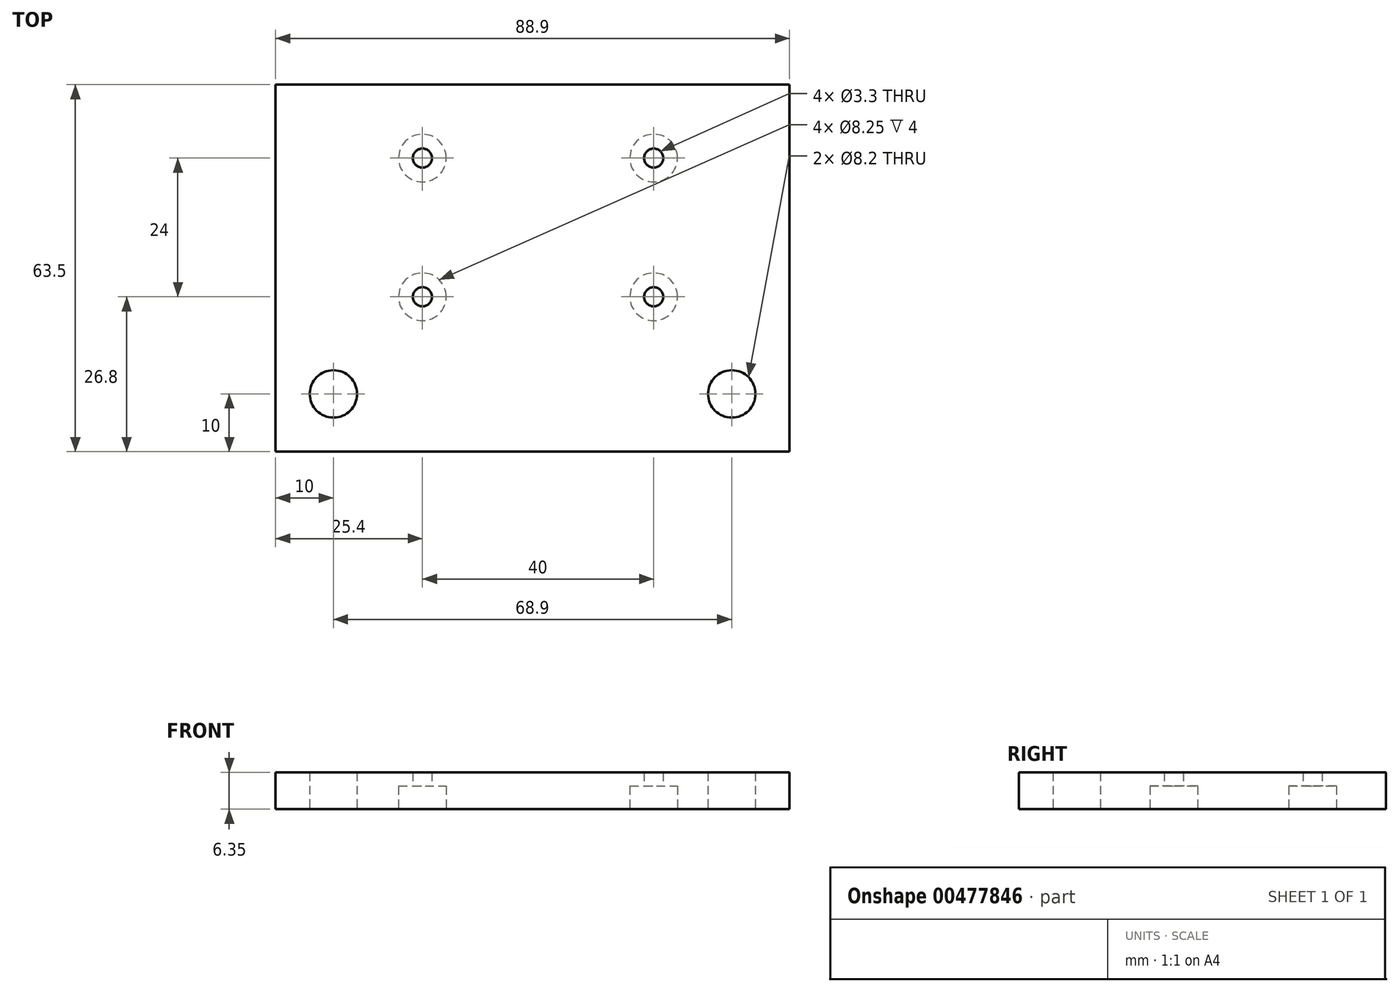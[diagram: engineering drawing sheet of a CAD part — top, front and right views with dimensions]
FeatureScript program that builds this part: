
annotation { "Feature Type Name" : "Feature", "Feature Type Description" : "" }
export const myFeature = defineFeature(function(context is Context, id is Id, definition is map)
    precondition{}
    {
        {
            var Q0;
            Q0=qCreatedBy(makeId("Top.planeOp"),FACE);
            var sketch = newSketch(context, id + "F0", { "sketchPlane" : qUnion([Q0])});
            skLineSegment(sketch, "E0.bottom", {"start": v(44.45, -31.75) * mm, "end": v(-44.45, -31.75) * mm});
            skLineSegment(sketch, "E0.top", {"start": v(44.45, 31.75) * mm, "end": v(-44.45, 31.75) * mm});
            skLineSegment(sketch, "E0.left", {"start": v(44.45, -31.75) * mm, "end": v(44.45, 31.75) * mm});
            skLineSegment(sketch, "E0.right", {"start": v(-44.45, -31.75) * mm, "end": v(-44.45, 31.75) * mm});
            skPoint(sketch, "E0.middle", {"position": v(0, 0) * mm});
            skPoint(sketch, "E1", {"position": v(-34.45, -21.75) * mm});
            skPoint(sketch, "E2.MirrorP", {"position": v(34.45, -21.75) * mm});
            skPoint(sketch, "E3", {"position": v(-19.05, 19.05) * mm});
            skPoint(sketch, "E4", {"position": v(-19.05, -4.95) * mm});
            skPoint(sketch, "E5", {"position": v(20.95, 19.05) * mm});
            skPoint(sketch, "E6", {"position": v(20.95, -4.95) * mm});
            skSolve(sketch);
        }
        {
            var Q0;
            Q0 = qSketchRegion(id + "F0", true);
            extrude(context, id + "F1", {"entities" : qUnion([Q0]), "depth" : 6.35 * mm});
        }
        {
            var Q0;
            Q0=sQuery(id+"F0.wireOp",VERTEX,"E1");
            var Q1;
            Q1=sQuery(id+"F0.wireOp",VERTEX,"E2.MirrorP");
            var Q2;
            Q2=makeQuery(id+"F1.opExtrude","SWEPT_BODY",BODY,{"disambiguationData":[OSD([sQuery(id+"F0.wireOp",EDGE,"E0.bottom"),sQuery(id+"F0.wireOp",EDGE,"E0.top"),sQuery(id+"F0.wireOp",EDGE,"E0.left"),sQuery(id+"F0.wireOp",EDGE,"E0.right")])]});
            hole(context, id + "F2", {"style" : HoleStyle.SIMPLE, "endStyle" : HoleEndStyle.THROUGH, "oppositeDirection" : true, "standardTappedOrClearance" : lookupTablePath({ "standard" : "ANSI", "fit" : "Close", "size" : "5/16", "type" : "Clearance" }), "standardBlindInLast" : lookupTablePath({ "fit" : "Close", "standard" : "ANSI", "size" : "5/16", "type" : "Clearance" }), "holeDiameter" : 8.2 * mm, "isTappedThrough" : true, "tappedDepth" : 12.7 * mm, "tapClearance" : 8, "startFromSketch" : true, "locations" : qUnion([Q0, Q1]), "scope" : qUnion([Q2])});
        }
        {
            var Q0;
            Q0=sQuery(id+"F0.wireOp",VERTEX,"E3");
            var Q1;
            Q1=sQuery(id+"F0.wireOp",VERTEX,"E4");
            var Q2;
            Q2=sQuery(id+"F0.wireOp",VERTEX,"9215ef34-4084-40ba-998e-ae7648b930f90.MirrorP");
            var Q3;
            Q3=sQuery(id+"F0.wireOp",VERTEX,"2579dafc-e9f0-4a31-a8d8-28c3b4851ec60.MirrorP");
            var Q4;
            Q4=sQuery(id+"F0.wireOp",VERTEX,"E5");
            var Q5;
            Q5=sQuery(id+"F0.wireOp",VERTEX,"E6");
            var Q6;
            Q6=makeQuery(id+"F1.opExtrude","SWEPT_BODY",BODY,{"disambiguationData":[OSD([sQuery(id+"F0.wireOp",EDGE,"E0.bottom"),sQuery(id+"F0.wireOp",EDGE,"E0.top"),sQuery(id+"F0.wireOp",EDGE,"E0.left"),sQuery(id+"F0.wireOp",EDGE,"E0.right")])]});
            hole(context, id + "F3", {"style" : HoleStyle.C_BORE, "endStyle" : HoleEndStyle.THROUGH, "oppositeDirection" : true, "standardTappedOrClearance" : lookupTablePath({ "standard" : "ISO", "engagement" : "75%", "pitch" : "0.7 mm", "size" : "M4", "type" : "Tapped" }), "standardBlindInLast" : lookupTablePath({ "standard" : "ISO", "engagement" : "75%", "pitch" : "0.7 mm", "size" : "M4", "type" : "Tapped" }), "holeDiameter" : 3.3 * mm, "cBoreDiameter" : 8.25 * mm, "cBoreDepth" : 4 * mm, "showTappedDepth" : true, "isTappedThrough" : true, "tappedDepth" : 12.7 * mm, "tapClearance" : 8, "startFromSketch" : true, "locations" : qUnion([Q0, Q1, Q2, Q3, Q4, Q5]), "scope" : qUnion([Q6]), "majorDiameter" : 4 * mm});
        }
    });
